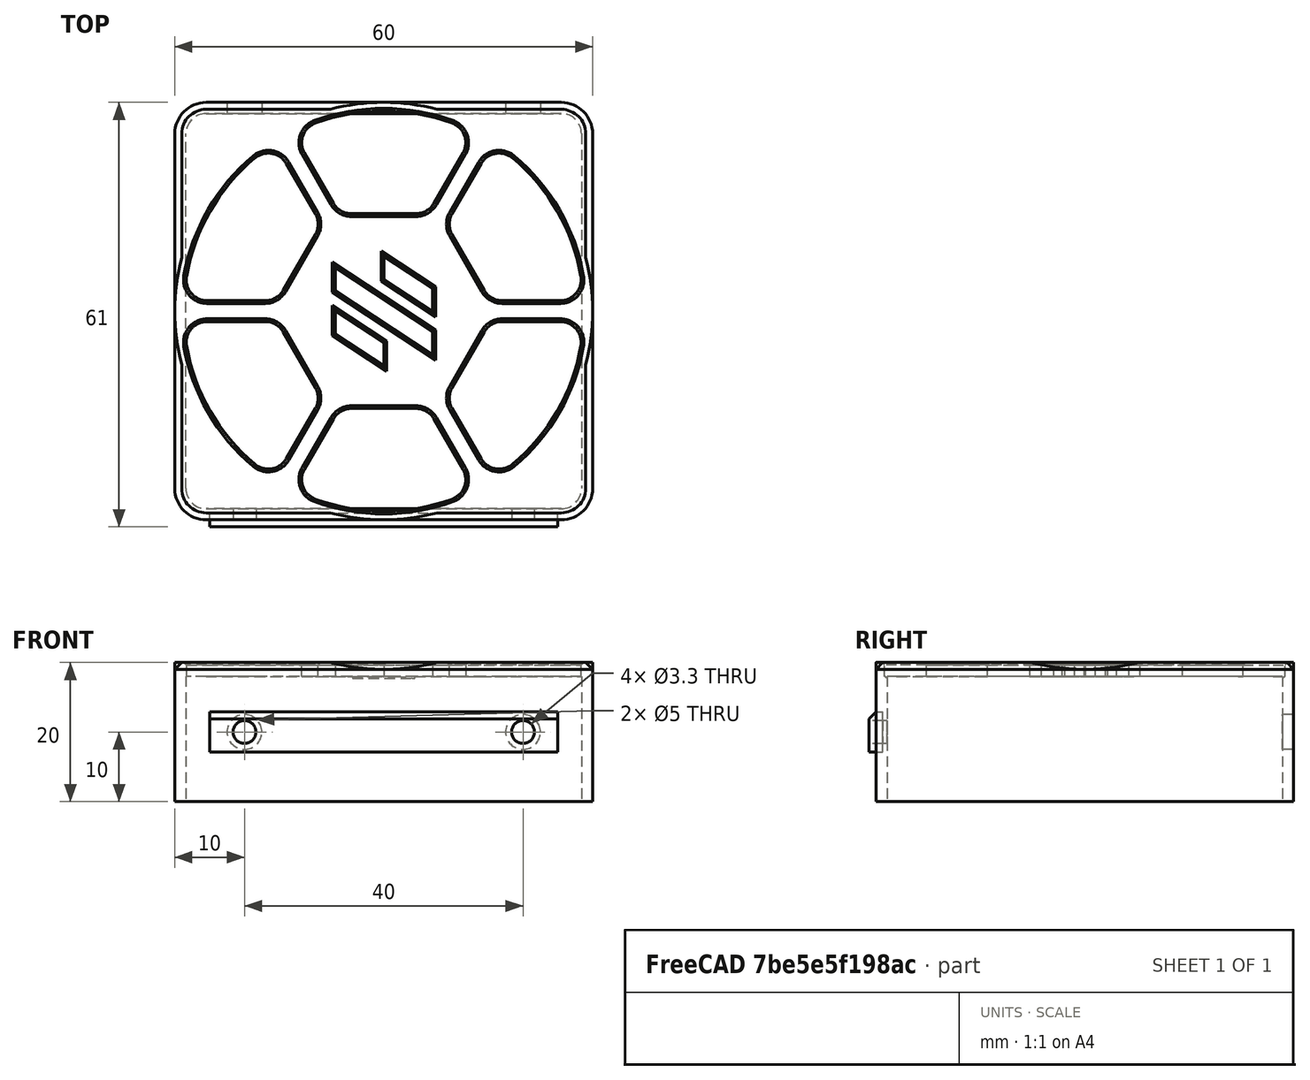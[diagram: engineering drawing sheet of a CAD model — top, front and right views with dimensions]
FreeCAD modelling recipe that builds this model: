
FCSTD DOCUMENT  (FreeCAD 0.18R16146 (Git))
Label: empty-fan-slot
License: Other
LicenseURL: GPL3
objects: Part::Cylinder×4, Part::Cut×3, Part::Feature×2, Part::MultiFuse×2, Part::Box×1, Part::Chamfer×1
note: 13 computed .brp shape members not serialized (recipe doc carries the construction recipe); baked Part::Feature solids carry a one-line shape summary decoded from their .brp

FEATURE [Part::Box] Box  label="Cube"
  AttacherType = Attacher::AttachEngine3D
  Height = 5.8
  Length = 50
  Placement = pos=(5,-1,7.1) rot=(0,0,1;0rad)
  Width = 2
FEATURE [Part::Feature] Part__Feature1605001  label="SOLID117"
  shape: bbox 60 x 60 x 20 mm, 159 faces (baked)
FEATURE [Part::Cylinder] Cylinder
  Angle = 360
  AttacherType = Attacher::AttachEngine3D
  Height = 10
  Placement = pos=(10,2.2e-15,10) rot=(1,0,0;1.5708rad)
  Radius = 1.65
FEATURE [Part::Chamfer] Chamfer
  Base = -> Box
  Edges = 1 edges r=1: [Edge10]
FEATURE [Part::Cylinder] Cylinder001
  Angle = 360
  AttacherType = Attacher::AttachEngine3D
  Height = 10
  Placement = pos=(50,2.2e-15,10) rot=(1,0,0;1.5708rad)
  Radius = 1.65
FEATURE [Part::MultiFuse] Fusion001
  Placement = pos=(0,5,0) rot=(0,0,1;0rad)
  Shapes = -> [Cylinder001,Cylinder]
FEATURE [Part::Feature] Fusion001001  label="Fusion002"
  Placement = pos=(0,5,0) rot=(0,0,1;0rad)
  shape: bbox 43.3 x 10 x 3.3 mm, 6 faces, 2 solids (baked)
FEATURE [Part::Cut] Cut
  Base = -> Chamfer
  Tool = -> Fusion001001
FEATURE [Part::Cut] Cut001
  Base = -> Part__Feature1605001
  Tool = -> Fusion001
FEATURE [Part::Cylinder] Cylinder002
  Angle = 360
  AttacherType = Attacher::AttachEngine3D
  Height = 10
  Placement = pos=(10,2.2e-15,10) rot=(1,0,0;1.5708rad)
  Radius = 2.5
FEATURE [Part::Cylinder] Cylinder003
  Angle = 360
  AttacherType = Attacher::AttachEngine3D
  Height = 10
  Placement = pos=(50,2.2e-15,10) rot=(1,0,0;1.5708rad)
  Radius = 2.5
FEATURE [Part::MultiFuse] Fusion
  Placement = pos=(0,63,0) rot=(0,0,1;0rad)
  Shapes = -> [Cylinder003,Cylinder002]
FEATURE [Part::Cut] Cut002
  Base = -> Cut001
  Tool = -> Fusion
